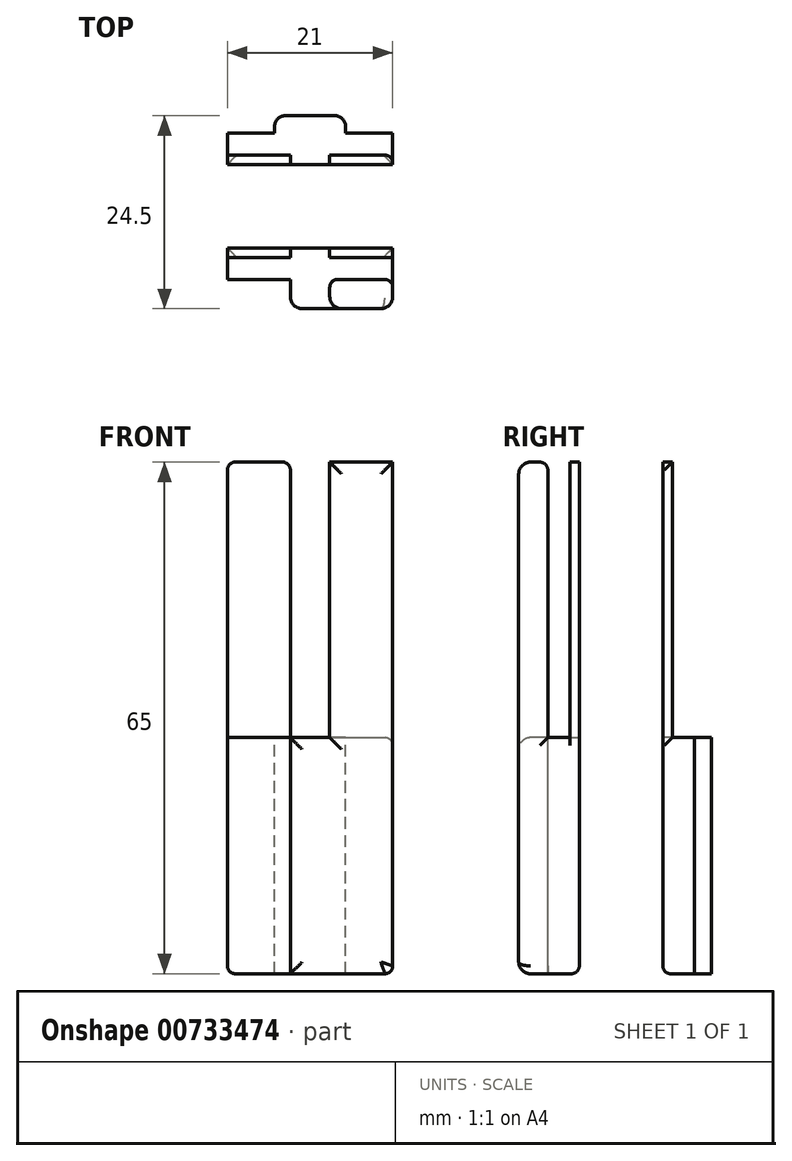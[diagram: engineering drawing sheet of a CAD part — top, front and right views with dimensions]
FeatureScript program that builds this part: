
annotation { "Feature Type Name" : "Feature", "Feature Type Description" : "" }
export const myFeature = defineFeature(function(context is Context, id is Id, definition is map)
    precondition{}
    {
        {
            var Q0;
            Q0=qCreatedBy(makeId("Top.planeOp"),FACE);
            var sketch = newSketch(context, id + "F0", { "sketchPlane" : qUnion([Q0])});
            skLineSegment(sketch, "E0.bottom", {"start": v(-10.5, -6.5) * mm, "end": v(10.5, -6.5) * mm});
            skLineSegment(sketch, "E0.top", {"start": v(-10.5, 6.5) * mm, "end": v(10.5, 6.5) * mm});
            skLineSegment(sketch, "E0.left", {"start": v(-10.5, -6.5) * mm, "end": v(-10.5, 6.5) * mm});
            skPoint(sketch, "E0.middle", {"position": v(0, 0) * mm});
            skLineSegment(sketch, "E1.bottom", {"start": v(-15, 13) * mm, "end": v(10.5, 13) * mm});
            skLineSegment(sketch, "E1.top", {"start": v(-15, -13) * mm, "end": v(10.5, -13) * mm});
            skLineSegment(sketch, "E1.left", {"start": v(-15, 13) * mm, "end": v(-15, -13) * mm});
            skLineSegment(sketch, "E2", {"start": v(10.5, 6.5) * mm, "end": v(10.5, 13) * mm});
            skLineSegment(sketch, "E3", {"start": v(10.5, -6.5) * mm, "end": v(10.5, -13) * mm});
            skPoint(sketch, "E1.right.start.orphan", {"position": v(15, 13) * mm});
            skPoint(sketch, "E4.orphan", {"position": v(15, -13) * mm});
            skLineSegment(sketch, "E5.MirrorCS", {"start": v(15, 13) * mm, "end": v(15, -13) * mm});
            skLineSegment(sketch, "E6.MirrorCS", {"start": v(15, 13) * mm, "end": v(-10.5, 13) * mm});
            skLineSegment(sketch, "E7.MirrorCS", {"start": v(15, -13) * mm, "end": v(-10.5, -13) * mm});
            skLineSegment(sketch, "E8.left", {"start": v(-4.5, 10.2) * mm, "end": v(-4.5, 6.5) * mm});
            skPoint(sketch, "E8.middle", {"position": v(0, 6.5) * mm});
            skLineSegment(sketch, "E9.left", {"start": v(-2.5, -6.5) * mm, "end": v(-2.5, -13) * mm});
            skLineSegment(sketch, "E9.right", {"start": v(2.5, -6.5) * mm, "end": v(2.5, -13) * mm});
            skPoint(sketch, "E9.middle", {"position": v(0, -13) * mm});
            skPoint(sketch, "E10.visualSharp", {"position": v(-4.5, 8.3) * mm});
            skArc(sketch, "E10.filletArc", {"start": v(-3.2, 11.5) * mm, "mid": v(-4.12, 11.12) * mm, "end": v(-4.5, 10.2) * mm});
            skPoint(sketch, "E11.visualSharp", {"position": v(4.53, 8.3) * mm});
            skLineSegment(sketch, "E12", {"start": v(-10.5, -6.5) * mm, "end": v(-10.5, -9.3) * mm});
            skArc(sketch, "E13.MirrorCS", {"start": v(3.2, 11.5) * mm, "mid": v(4.12, 11.12) * mm, "end": v(4.5, 10.2) * mm});
            skLineSegment(sketch, "E14.MirrorCS", {"start": v(4.5, 10.2) * mm, "end": v(4.5, 6.5) * mm});
            skLineSegment(sketch, "E15", {"start": v(-3.2, 11.5) * mm, "end": v(3.2, 11.5) * mm});
            skLineSegment(sketch, "E16", {"start": v(-10.5, -9.3) * mm, "end": v(10.5, -9.3) * mm});
            skLineSegment(sketch, "E17.MirrorCS", {"start": v(-10.5, 6.5) * mm, "end": v(-10.5, 9.3) * mm});
            skLineSegment(sketch, "E18.MirrorCS", {"start": v(-10.5, 9.3) * mm, "end": v(10.5, 9.3) * mm});
            skLineSegment(sketch, "E19", {"start": v(10.5, 6.5) * mm, "end": v(10.5, -6.5) * mm});
            skLineSegment(sketch, "E20.bottom", {"start": v(-10.5, 5.3) * mm, "end": v(10.5, 5.3) * mm});
            skLineSegment(sketch, "E20.top", {"start": v(-10.5, -5.3) * mm, "end": v(10.5, -5.3) * mm});
            skLineSegment(sketch, "E20.left", {"start": v(-10.5, 5.3) * mm, "end": v(-10.5, -5.3) * mm});
            skLineSegment(sketch, "E20.right", {"start": v(10.5, 5.3) * mm, "end": v(10.5, -5.3) * mm});
            skLineSegment(sketch, "E21", {"start": v(-2.5, -6.5) * mm, "end": v(-2.5, -5.3) * mm});
            skLineSegment(sketch, "E22", {"start": v(2.5, -6.5) * mm, "end": v(2.5, -5.3) * mm});
            skLineSegment(sketch, "E23.MirrorCS", {"start": v(-2.5, 6.5) * mm, "end": v(-2.5, 5.3) * mm});
            skLineSegment(sketch, "E24.MirrorCS", {"start": v(2.5, 6.5) * mm, "end": v(2.5, 5.3) * mm});
            skSolve(sketch);
        }
        {
            var Q0;
            {var subQ10=sQuery(id+"F0.wireOp",EDGE,"E1.left");var subQ12=sQuery(id+"F0.wireOp",EDGE,"E1.top");var subQ41=sQuery(id+"F0.wireOp",EDGE,"E9.right");var subQ42=makeQuery(id+"F0.imprint","INTERSECT",VERTEX,{"derivedFrom":[subQ12,subQ41]});var subQ44=makeQuery(id+"F0.imprint","IMPRINT",EDGE,{"disambiguationData":[TD([[subQ42,1.0]])],"derivedFrom":subQ41});Q0=qUnion([makeQuery(id+"F0.imprint","IMPRINT",FACE,{"disambiguationData":[TD([[subQ44,1.0]])]}),makeQuery(id+"F0.imprint","IMPRINT",FACE,{"disambiguationData":[TD([[makeQuery(id+"F0.imprint","IMPRINT",EDGE,{"disambiguationData":[TD([[subQ42,1.0]])],"derivedFrom":subQ12}),1.0]])]}),makeQuery(id+"F0.imprint","IMPRINT",FACE,{"disambiguationData":[TD([[makeQuery(id+"F0.imprint","IMPRINT",EDGE,{"derivedFrom":sQuery(id+"F0.wireOp",EDGE,"E5.MirrorCS")}),-1.0]])]}),makeQuery(id+"F0.imprint","IMPRINT",FACE,{"disambiguationData":[TD([[makeQuery(id+"F0.imprint","IMPRINT",EDGE,{"derivedFrom":subQ10}),1.0]])]})]);}
            var Q1;
            {var subQ0=sQuery(id+"F0.wireOp",EDGE,"E17.MirrorCS");Q1=makeQuery(id+"F0.imprint","IMPRINT",FACE,{"disambiguationData":[TD([[makeQuery(id+"F0.imprint","IMPRINT",EDGE,{"derivedFrom":subQ0}),-1.0]])]});}
            var Q2;
            {var subQ0=sQuery(id+"F0.wireOp",EDGE,"E0.top");var subQ1=makeQuery(id+"F0.imprint","INTERSECT",VERTEX,{"derivedFrom":[subQ0,sQuery(id+"F0.wireOp",EDGE,"E23.MirrorCS")]});Q2=makeQuery(id+"F0.imprint","IMPRINT",FACE,{"disambiguationData":[TD([[makeQuery(id+"F0.imprint","IMPRINT",EDGE,{"disambiguationData":[TD([[subQ1,-1.0]])],"derivedFrom":subQ0}),1.0]])]});}
            var Q3;
            {var subQ4=sQuery(id+"F0.wireOp",EDGE,"E10.filletArc");Q3=makeQuery(id+"F0.imprint","IMPRINT",FACE,{"disambiguationData":[TD([[makeQuery(id+"F0.imprint","IMPRINT",EDGE,{"derivedFrom":subQ4}),1.0]])]});}
            var Q4;
            {var subQ0=sQuery(id+"F0.wireOp",EDGE,"E14.MirrorCS");var subQ5=sQuery(id+"F0.wireOp",EDGE,"E18.MirrorCS");var subQ7=makeQuery(id+"F0.imprint","INTERSECT",VERTEX,{"derivedFrom":[subQ0,subQ5]});Q4=makeQuery(id+"F0.imprint","IMPRINT",FACE,{"disambiguationData":[TD([[makeQuery(id+"F0.imprint","IMPRINT",EDGE,{"disambiguationData":[TD([[subQ7,-1.0]])],"derivedFrom":subQ0}),1.0]])]});}
            var Q5;
            {var subQ3=sQuery(id+"F0.wireOp",EDGE,"E3");var subQ5=sQuery(id+"F0.wireOp",EDGE,"E16");var subQ7=makeQuery(id+"F0.imprint","INTERSECT",VERTEX,{"derivedFrom":[subQ3,subQ5]});Q5=makeQuery(id+"F0.imprint","IMPRINT",FACE,{"disambiguationData":[TD([[makeQuery(id+"F0.imprint","IMPRINT",EDGE,{"disambiguationData":[TD([[subQ7,1.0]])],"derivedFrom":subQ5}),1.0]])]});}
            var Q6;
            {var subQ3=sQuery(id+"F0.wireOp",EDGE,"E9.left");var subQ5=sQuery(id+"F0.wireOp",EDGE,"E16");var subQ6=makeQuery(id+"F0.imprint","INTERSECT",VERTEX,{"derivedFrom":[subQ3,subQ5]});Q6=makeQuery(id+"F0.imprint","IMPRINT",FACE,{"disambiguationData":[TD([[makeQuery(id+"F0.imprint","IMPRINT",EDGE,{"disambiguationData":[TD([[subQ6,-1.0]])],"derivedFrom":subQ5}),1.0]])]});}
            var Q7;
            {var subQ0=sQuery(id+"F0.wireOp",EDGE,"E12");Q7=makeQuery(id+"F0.imprint","IMPRINT",FACE,{"disambiguationData":[TD([[makeQuery(id+"F0.imprint","IMPRINT",EDGE,{"derivedFrom":subQ0}),1.0]])]});}
            var Q8;
            {var subQ3=sQuery(id+"F0.wireOp",EDGE,"m3D1H77D-jmqX-7KNN-ilgy-fV066lonf65t");Q8=makeQuery(id+"F0.imprint","IMPRINT",FACE,{"disambiguationData":[TD([[makeQuery(id+"F0.imprint","IMPRINT",EDGE,{"derivedFrom":subQ3}),-1.0]])]});}
            var Q9;
            {var subQ0=sQuery(id+"F0.wireOp",EDGE,"m3D1H77D-jmqX-7KNN-ilgy-fV066lonf65t");Q9=makeQuery(id+"F0.imprint","IMPRINT",FACE,{"disambiguationData":[TD([[makeQuery(id+"F0.imprint","IMPRINT",EDGE,{"derivedFrom":subQ0}),1.0]])]});}
            var Q10;
            {var subQ3=sQuery(id+"F0.wireOp",EDGE,"p7ErZm02-1nuq-MqLj-lWC7-7FAkOLW2AWz5");Q10=makeQuery(id+"F0.imprint","IMPRINT",FACE,{"disambiguationData":[TD([[makeQuery(id+"F0.imprint","IMPRINT",EDGE,{"derivedFrom":subQ3}),1.0]])]});}
            var Q11;
            {var subQ0=sQuery(id+"F0.wireOp",EDGE,"E22");Q11=makeQuery(id+"F0.imprint","IMPRINT",FACE,{"disambiguationData":[TD([[makeQuery(id+"F0.imprint","IMPRINT",EDGE,{"derivedFrom":subQ0}),-1.0]])]});}
            var Q12;
            {var subQ2=sQuery(id+"F0.wireOp",EDGE,"E21");Q12=makeQuery(id+"F0.imprint","IMPRINT",FACE,{"disambiguationData":[TD([[makeQuery(id+"F0.imprint","IMPRINT",EDGE,{"derivedFrom":subQ2}),-1.0]])]});}
            var Q13;
            {var subQ3=sQuery(id+"F0.wireOp",EDGE,"E21");Q13=makeQuery(id+"F0.imprint","IMPRINT",FACE,{"disambiguationData":[TD([[makeQuery(id+"F0.imprint","IMPRINT",EDGE,{"derivedFrom":subQ3}),1.0]])]});}
            var Q14;
            {var subQ5=sQuery(id+"F0.wireOp",EDGE,"E23.MirrorCS");Q14=makeQuery(id+"F0.imprint","IMPRINT",FACE,{"disambiguationData":[TD([[makeQuery(id+"F0.imprint","IMPRINT",EDGE,{"derivedFrom":subQ5}),-1.0]])]});}
            var Q15;
            {var subQ0=sQuery(id+"F0.wireOp",EDGE,"E23.MirrorCS");Q15=makeQuery(id+"F0.imprint","IMPRINT",FACE,{"disambiguationData":[TD([[makeQuery(id+"F0.imprint","IMPRINT",EDGE,{"derivedFrom":subQ0}),1.0]])]});}
            var Q16;
            {var subQ3=sQuery(id+"F0.wireOp",EDGE,"E24.MirrorCS");Q16=makeQuery(id+"F0.imprint","IMPRINT",FACE,{"disambiguationData":[TD([[makeQuery(id+"F0.imprint","IMPRINT",EDGE,{"derivedFrom":subQ3}),1.0]])]});}
            extrude(context, id + "F1", {"entities" : qUnion([Q0, Q1, Q2, Q3, Q4, Q5, Q6, Q7, Q8, Q9, Q10, Q11, Q12, Q13, Q14, Q15, Q16]), "oppositeDirection" : true, "depth" : 30 * mm, "offsetDistance" : 25 * mm});
        }
        {
            var Q0;
            {var subQ8=sQuery(id+"F0.wireOp",EDGE,"E1.left");Q0=makeQuery(id+"F0.imprint","IMPRINT",FACE,{"disambiguationData":[TD([[makeQuery(id+"F0.imprint","IMPRINT",EDGE,{"derivedFrom":subQ8}),1.0]])]});}
            var Q1;
            {var subQ0=sQuery(id+"F0.wireOp",EDGE,"E9.right");var subQ1=sQuery(id+"F0.wireOp",EDGE,"E1.top");var subQ2=makeQuery(id+"F0.imprint","INTERSECT",VERTEX,{"derivedFrom":[subQ1,subQ0]});Q1=makeQuery(id+"F0.imprint","IMPRINT",FACE,{"disambiguationData":[TD([[makeQuery(id+"F0.imprint","IMPRINT",EDGE,{"disambiguationData":[TD([[subQ2,1.0]])],"derivedFrom":subQ0}),1.0]])]});}
            var Q2;
            {var subQ3=sQuery(id+"F0.wireOp",EDGE,"m3D1H77D-jmqX-7KNN-ilgy-fV066lonf65t");Q2=makeQuery(id+"F0.imprint","IMPRINT",FACE,{"disambiguationData":[TD([[makeQuery(id+"F0.imprint","IMPRINT",EDGE,{"derivedFrom":subQ3}),-1.0]])]});}
            var Q3;
            {var subQ3=sQuery(id+"F0.wireOp",EDGE,"p7ErZm02-1nuq-MqLj-lWC7-7FAkOLW2AWz5");Q3=makeQuery(id+"F0.imprint","IMPRINT",FACE,{"disambiguationData":[TD([[makeQuery(id+"F0.imprint","IMPRINT",EDGE,{"derivedFrom":subQ3}),1.0]])]});}
            var Q4;
            {var subQ0=sQuery(id+"F0.wireOp",EDGE,"E22");Q4=makeQuery(id+"F0.imprint","IMPRINT",FACE,{"disambiguationData":[TD([[makeQuery(id+"F0.imprint","IMPRINT",EDGE,{"derivedFrom":subQ0}),-1.0]])]});}
            var Q5;
            {var subQ3=sQuery(id+"F0.wireOp",EDGE,"E21");Q5=makeQuery(id+"F0.imprint","IMPRINT",FACE,{"disambiguationData":[TD([[makeQuery(id+"F0.imprint","IMPRINT",EDGE,{"derivedFrom":subQ3}),1.0]])]});}
            var Q6;
            {var subQ5=sQuery(id+"F0.wireOp",EDGE,"E23.MirrorCS");Q6=makeQuery(id+"F0.imprint","IMPRINT",FACE,{"disambiguationData":[TD([[makeQuery(id+"F0.imprint","IMPRINT",EDGE,{"derivedFrom":subQ5}),-1.0]])]});}
            var Q7;
            {var subQ3=sQuery(id+"F0.wireOp",EDGE,"E24.MirrorCS");Q7=makeQuery(id+"F0.imprint","IMPRINT",FACE,{"disambiguationData":[TD([[makeQuery(id+"F0.imprint","IMPRINT",EDGE,{"derivedFrom":subQ3}),1.0]])]});}
            extrude(context, id + "F2", {"entities" : qUnion([Q0, Q1, Q2, Q3, Q4, Q5, Q6, Q7]), "operationType" : NewBodyOperationType.ADD, "depth" : 35 * mm, "offsetDistance" : 25 * mm});
        }
        {
            var Q0;
            Q0=makeQuery(id+"F2.opExtrude","CAP_EDGE",EDGE,{"disambiguationData":[OSD([sQuery(id+"F0.wireOp",EDGE,"E1.left")])],"isStart":false});
            var Q1;
            Q1=makeQuery(id+"F1.opExtrude","CAP_EDGE",EDGE,{"disambiguationData":[OSD([sQuery(id+"F0.wireOp",EDGE,"E1.left")])],"isStart":false});
            var Q2;
            {var subQ0=sQuery(id+"F0.wireOp",EDGE,"E1.left");var subQ1=sQuery(id+"F0.wireOp",EDGE,"E1.bottom");Q2=makeQuery(id+"F2.boolean.opBoolean","MERGE",EDGE,{"derivedFrom":[makeQuery(id+"F1.opExtrude","SWEPT_EDGE",EDGE,{"disambiguationData":[OSD([subQ1,subQ0])]}),makeQuery(id+"F2.opExtrude","SWEPT_EDGE",EDGE,{"disambiguationData":[OSD([subQ1,subQ0])]})]});}
            var Q3;
            {var subQ0=sQuery(id+"F0.wireOp",EDGE,"E1.left");var subQ1=sQuery(id+"F0.wireOp",EDGE,"E1.top");Q3=makeQuery(id+"F2.boolean.opBoolean","MERGE",EDGE,{"derivedFrom":[makeQuery(id+"F1.opExtrude","SWEPT_EDGE",EDGE,{"disambiguationData":[OSD([subQ1,subQ0])]}),makeQuery(id+"F2.opExtrude","SWEPT_EDGE",EDGE,{"disambiguationData":[OSD([subQ1,subQ0])]})]});}
            var Q4;
            Q4=makeQuery(id+"F1.opExtrude","SWEPT_EDGE",EDGE,{"disambiguationData":[OSD([sQuery(id+"F0.wireOp",EDGE,"E5.MirrorCS"),sQuery(id+"F0.wireOp",EDGE,"E6.MirrorCS")])]});
            var Q5;
            Q5=makeQuery(id+"F1.opExtrude","CAP_EDGE",EDGE,{"disambiguationData":[OSD([sQuery(id+"F0.wireOp",EDGE,"E1.bottom"),sQuery(id+"F0.wireOp",EDGE,"E6.MirrorCS")])],"isStart":false});
            var Q6;
            {var subQ0=sQuery(id+"F0.wireOp",EDGE,"E1.bottom");Q6=makeQuery(id+"F2.boolean.opBoolean","MERGE",FACE,{"derivedFrom":[makeQuery(id+"F1.opExtrude","SWEPT_FACE",FACE,{"disambiguationData":[OSD([subQ0,sQuery(id+"F0.wireOp",EDGE,"E6.MirrorCS")])]}),makeQuery(id+"F2.opExtrude","SWEPT_FACE",FACE,{"disambiguationData":[OSD([subQ0])]})]});}
            var Q7;
            {var subQ0=sQuery(id+"F0.wireOp",EDGE,"E1.top");var subQ1=makeQuery(id+"F0.imprint","IMPRINT",VERTEX,{"derivedFrom":subQ0});var subQ2=sQuery(id+"F0.wireOp",EDGE,"E7.MirrorCS");Q7=makeQuery(id+"F2.boolean.opBoolean","MERGE",FACE,{"derivedFrom":[makeQuery(id+"F1.opExtrude","SWEPT_FACE",FACE,{"disambiguationData":[OSD([subQ0,subQ2])]}),makeQuery(id+"F2.opExtrude","SWEPT_FACE",FACE,{"disambiguationData":[OSD([subQ0]),TDD([makeQuery(id+"F0.imprint","IMPRINT",EDGE,{"disambiguationData":[TD([[makeQuery(id+"F0.imprint","INTERSECT",VERTEX,{"derivedFrom":[subQ0,sQuery(id+"F0.wireOp",EDGE,"E9.right")]}),-1.0]])],"derivedFrom":subQ0})])]}),makeQuery(id+"F2.opExtrude","SWEPT_FACE",FACE,{"disambiguationData":[OSD([subQ0]),TDD([makeQuery(id+"F0.imprint","IMPRINT",EDGE,{"disambiguationData":[TD([[subQ1,-1.0]])],"derivedFrom":subQ0}),makeQuery(id+"F0.imprint","IMPRINT",EDGE,{"disambiguationData":[TD([[subQ1,1.0]])],"derivedFrom":subQ0})])]})]});}
            var Q8;
            Q8=makeQuery(id+"F1.opExtrude","SWEPT_FACE",FACE,{"disambiguationData":[OSD([sQuery(id+"F0.wireOp",EDGE,"E5.MirrorCS")])]});
            fillet(context, id + "F3", {"entities" : qUnion([Q0, Q1, Q2, Q3, Q4, Q5, Q6, Q7, Q8]), "radius" : 1.5 * mm, "tangentPropagation" : true, "allowEdgeOverflow" : false});
        }
        {
            var Q0;
            Q0=makeQuery(id+"F1.opExtrude","CAP_EDGE",EDGE,{"disambiguationData":[OSD([sQuery(id+"F0.wireOp",EDGE,"E0.bottom")])],"isStart":true});
            var Q1;
            Q1=makeQuery(id+"F1.opExtrude","CAP_EDGE",EDGE,{"disambiguationData":[OSD([sQuery(id+"F0.wireOp",EDGE,"E0.bottom")])],"isStart":false});
            var Q2;
            Q2=makeQuery(id+"F1.opExtrude","CAP_EDGE",EDGE,{"disambiguationData":[OSD([sQuery(id+"F0.wireOp",EDGE,"E0.top")])],"isStart":true});
            var Q3;
            Q3=makeQuery(id+"F1.opExtrude","CAP_EDGE",EDGE,{"disambiguationData":[OSD([sQuery(id+"F0.wireOp",EDGE,"E0.top")])],"isStart":false});
            var Q4;
            Q4=makeQuery(id+"F1.opExtrude","CAP_EDGE",EDGE,{"disambiguationData":[OSD([sQuery(id+"F0.wireOp",EDGE,"E19")])],"isStart":true});
            var Q5;
            Q5=makeQuery(id+"F1.opExtrude","CAP_EDGE",EDGE,{"disambiguationData":[OSD([sQuery(id+"F0.wireOp",EDGE,"E19")])],"isStart":false});
            var Q6;
            Q6=makeQuery(id+"F1.opExtrude","CAP_EDGE",EDGE,{"disambiguationData":[OSD([sQuery(id+"F0.wireOp",EDGE,"E0.left")])],"isStart":false});
            var Q7;
            Q7=makeQuery(id+"F2.opExtrude","SWEPT_EDGE",EDGE,{"disambiguationData":[OSD([sQuery(id+"F0.wireOp",EDGE,"E3"),sQuery(id+"F0.wireOp",EDGE,"E16")])]});
            var Q8;
            Q8=makeQuery(id+"F2.opExtrude","SWEPT_EDGE",EDGE,{"disambiguationData":[OSD([sQuery(id+"F0.wireOp",EDGE,"E2"),sQuery(id+"F0.wireOp",EDGE,"E18.MirrorCS")])]});
            var Q9;
            {var subQ0=sQuery(id+"F0.wireOp",EDGE,"E16");Q9=makeQuery(id+"F2.opExtrude","CAP_EDGE",EDGE,{"disambiguationData":[OSD([subQ0]),TDD([makeQuery(id+"F0.imprint","IMPRINT",EDGE,{"disambiguationData":[TD([[makeQuery(id+"F0.imprint","INTERSECT",VERTEX,{"derivedFrom":[sQuery(id+"F0.wireOp",EDGE,"E3"),subQ0]}),1.0]])],"derivedFrom":subQ0})])],"isStart":false});}
            var Q10;
            Q10=makeQuery(id+"F2.opExtrude","SWEPT_EDGE",EDGE,{"disambiguationData":[OSD([sQuery(id+"F0.wireOp",EDGE,"E9.left"),sQuery(id+"F0.wireOp",EDGE,"E16")])]});
            var Q11;
            Q11=makeQuery(id+"F2.opExtrude","SWEPT_EDGE",EDGE,{"disambiguationData":[OSD([sQuery(id+"F0.wireOp",EDGE,"E9.right"),sQuery(id+"F0.wireOp",EDGE,"E16")])]});
            var Q12;
            {var subQ0=sQuery(id+"F0.wireOp",EDGE,"E16");Q12=makeQuery(id+"F2.opExtrude","CAP_EDGE",EDGE,{"disambiguationData":[OSD([subQ0]),TDD([makeQuery(id+"F0.imprint","IMPRINT",EDGE,{"disambiguationData":[TD([[makeQuery(id+"F0.imprint","INTERSECT",VERTEX,{"derivedFrom":[sQuery(id+"F0.wireOp",EDGE,"E9.left"),subQ0]}),1.0]])],"derivedFrom":subQ0})])],"isStart":false});}
            var Q13;
            {var subQ0=sQuery(id+"F0.wireOp",EDGE,"E18.MirrorCS");Q13=makeQuery(id+"F2.opExtrude","CAP_EDGE",EDGE,{"disambiguationData":[OSD([subQ0]),TDD([makeQuery(id+"F0.imprint","IMPRINT",EDGE,{"disambiguationData":[TD([[makeQuery(id+"F0.imprint","INTERSECT",VERTEX,{"derivedFrom":[sQuery(id+"F0.wireOp",EDGE,"E2"),subQ0]}),1.0]])],"derivedFrom":subQ0})])],"isStart":false});}
            var Q14;
            {var subQ0=sQuery(id+"F0.wireOp",EDGE,"E18.MirrorCS");Q14=makeQuery(id+"F2.opExtrude","CAP_EDGE",EDGE,{"disambiguationData":[OSD([subQ0]),TDD([makeQuery(id+"F0.imprint","IMPRINT",EDGE,{"disambiguationData":[TD([[makeQuery(id+"F0.imprint","INTERSECT",VERTEX,{"derivedFrom":[sQuery(id+"F0.wireOp",EDGE,"E8.left"),subQ0]}),1.0]])],"derivedFrom":subQ0})])],"isStart":false});}
            var Q15;
            Q15=makeQuery(id+"F2.opExtrude","CAP_EDGE",EDGE,{"disambiguationData":[OSD([sQuery(id+"F0.wireOp",EDGE,"E0.left")])],"isStart":false});
            var Q16;
            Q16=makeQuery(id+"F2.opExtrude","CAP_EDGE",EDGE,{"disambiguationData":[OSD([sQuery(id+"F0.wireOp",EDGE,"E17.MirrorCS")])],"isStart":false});
            var Q17;
            Q17=makeQuery(id+"F2.opExtrude","CAP_EDGE",EDGE,{"disambiguationData":[OSD([sQuery(id+"F0.wireOp",EDGE,"E12")])],"isStart":false});
            var Q18;
            Q18=makeQuery(id+"F2.opExtrude","CAP_EDGE",EDGE,{"disambiguationData":[OSD([sQuery(id+"F0.wireOp",EDGE,"E0.left")])],"isStart":false});
            var Q19;
            Q19=makeQuery(id+"F2.opExtrude","CAP_EDGE",EDGE,{"disambiguationData":[OSD([sQuery(id+"F0.wireOp",EDGE,"E23.MirrorCS")])],"isStart":false});
            var Q20;
            Q20=makeQuery(id+"F2.opExtrude","CAP_EDGE",EDGE,{"disambiguationData":[OSD([sQuery(id+"F0.wireOp",EDGE,"E24.MirrorCS")])],"isStart":false});
            var Q21;
            {var subQ0=sQuery(id+"F0.wireOp",EDGE,"E19");Q21=makeQuery(id+"F2.opExtrude","CAP_EDGE",EDGE,{"disambiguationData":[OSD([subQ0]),TDD([makeQuery(id+"F0.imprint","IMPRINT",EDGE,{"disambiguationData":[TD([[makeQuery(id+"F0.imprint","INTERSECT",VERTEX,{"derivedFrom":[subQ0,sQuery(id+"F0.wireOp",EDGE,"E20.bottom")]}),1.0]])],"derivedFrom":subQ0})])],"isStart":false});}
            var Q22;
            {var subQ0=sQuery(id+"F0.wireOp",EDGE,"E19");Q22=makeQuery(id+"F2.opExtrude","CAP_EDGE",EDGE,{"disambiguationData":[OSD([subQ0]),TDD([makeQuery(id+"F0.imprint","IMPRINT",EDGE,{"disambiguationData":[TD([[makeQuery(id+"F0.imprint","INTERSECT",VERTEX,{"derivedFrom":[subQ0,sQuery(id+"F0.wireOp",EDGE,"E20.top")]}),-1.0]])],"derivedFrom":subQ0})])],"isStart":false});}
            var Q23;
            Q23=makeQuery(id+"F2.opExtrude","CAP_EDGE",EDGE,{"disambiguationData":[OSD([sQuery(id+"F0.wireOp",EDGE,"E22")])],"isStart":false});
            var Q24;
            Q24=makeQuery(id+"F2.opExtrude","CAP_EDGE",EDGE,{"disambiguationData":[OSD([sQuery(id+"F0.wireOp",EDGE,"E21")])],"isStart":false});
            var Q25;
            Q25=makeQuery(id+"F1.opExtrude","CAP_EDGE",EDGE,{"disambiguationData":[OSD([sQuery(id+"F0.wireOp",EDGE,"E19")])],"isStart":true});
            var Q26;
            Q26=makeQuery(id+"F1.opExtrude","CAP_EDGE",EDGE,{"disambiguationData":[OSD([sQuery(id+"F0.wireOp",EDGE,"E20.bottom")])],"isStart":false});
            var Q27;
            Q27=makeQuery(id+"F1.opExtrude","CAP_EDGE",EDGE,{"disambiguationData":[OSD([sQuery(id+"F0.wireOp",EDGE,"E19")])],"isStart":false});
            var Q28;
            Q28=makeQuery(id+"F1.opExtrude","CAP_EDGE",EDGE,{"disambiguationData":[OSD([sQuery(id+"F0.wireOp",EDGE,"E20.top")])],"isStart":false});
            var Q29;
            Q29=makeQuery(id+"F1.opExtrude","CAP_EDGE",EDGE,{"disambiguationData":[OSD([sQuery(id+"F0.wireOp",EDGE,"E0.left")])],"isStart":false});
            fillet(context, id + "F4", {"entities" : qUnion([Q0, Q1, Q2, Q3, Q4, Q5, Q6, Q7, Q8, Q9, Q10, Q11, Q12, Q13, Q14, Q15, Q16, Q17, Q18, Q19, Q20, Q21, Q22, Q23, Q24, Q25, Q26, Q27, Q28, Q29]), "radius" : 1 * mm, "tangentPropagation" : true, "allowEdgeOverflow" : false});
        }
    });
